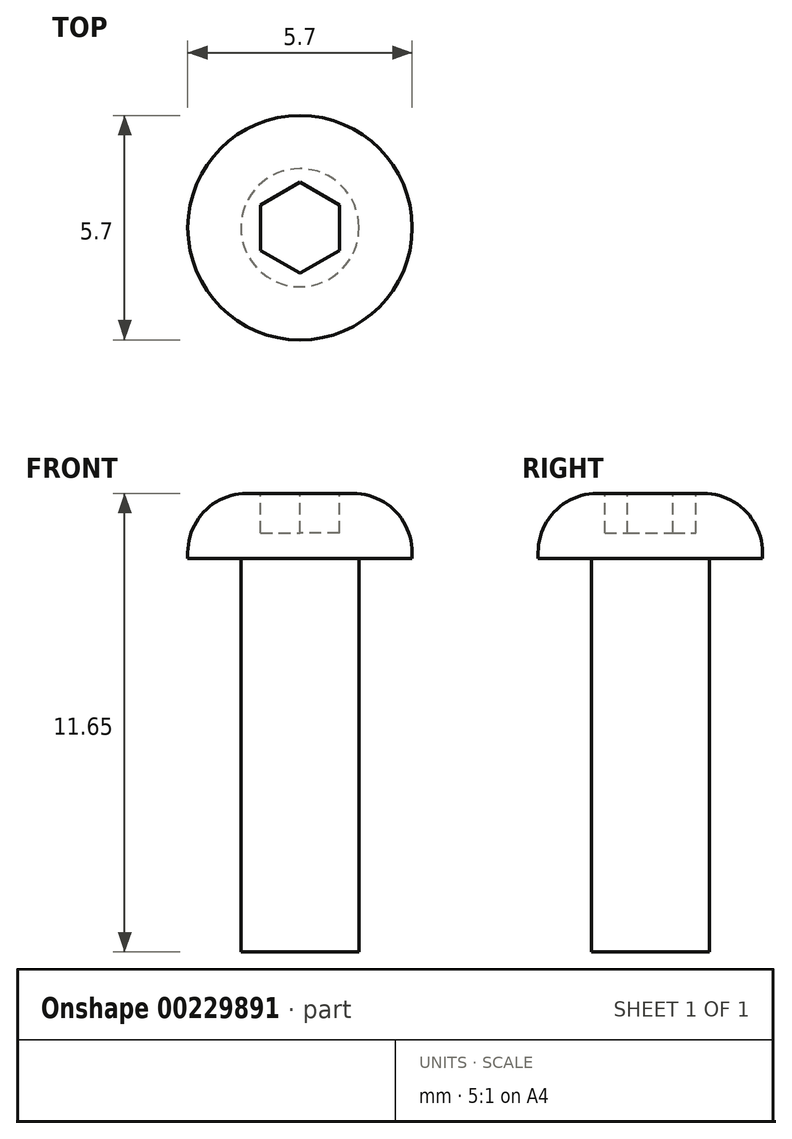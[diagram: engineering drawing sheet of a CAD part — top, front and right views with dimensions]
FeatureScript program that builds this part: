
annotation { "Feature Type Name" : "Feature", "Feature Type Description" : "" }
export const myFeature = defineFeature(function(context is Context, id is Id, definition is map)
    precondition{}
    {
        {
            var Q0;
            Q0=qCreatedBy(makeId("Top.planeOp"),FACE);
            var sketch = newSketch(context, id + "F0", { "sketchPlane" : qUnion([Q0])});
            skCircle(sketch, "E0", {"center": v(0, 0) * mm, "radius": 2.85 * mm});
            skCircle(sketch, "E1", {"center": v(0, 0) * mm, "radius": 1.5 * mm});
            skSolve(sketch);
        }
        {
            var Q0;
            Q0=makeQuery(id+"F0.imprint","IMPRINT",FACE,{"disambiguationData":[TD([[makeQuery(id+"F0.imprint","IMPRINT",EDGE,{"derivedFrom":sQuery(id+"F0.wireOp",EDGE,"E1")}),1.0]])]});
            extrude(context, id + "F1", {"entities" : qUnion([Q0]), "oppositeDirection" : true, "depth" : 10 * mm});
        }
        {
            var Q0;
            Q0 = qSketchRegion(id + "F0", true);
            var Q1;
            Q1=makeQuery(id+"F1.opExtrude","CAP_FACE",FACE,{"disambiguationData":[OSD([sQuery(id+"F0.wireOp",EDGE,"E1")])],"isStart":true});
            extrude(context, id + "F2", {"entities" : qUnion([Q0, Q1]), "operationType" : NewBodyOperationType.ADD, "depth" : 1.65 * mm});
        }
        {
            var Q0;
            {var subQ0=sQuery(id+"F0.wireOp",EDGE,"E1");Q0=makeQuery(id+"F2.boolean.opBoolean","MERGE",FACE,{"derivedFrom":[makeQuery(id+"F2.opExtrude","CAP_FACE",FACE,{"disambiguationData":[OSD([sQuery(id+"F0.wireOp",EDGE,"E0"),subQ0])],"isStart":false}),makeQuery(id+"F2.opExtrude","CAP_FACE",FACE,{"disambiguationData":[OSD([subQ0])],"isStart":false})]});}
            var sketch = newSketch(context, id + "F3", { "sketchPlane" : qUnion([Q0])});
            skCircle(sketch, "E2.cCircle", {"center": v(0, 0) * mm, "radius": 1 * mm, "construction": true});
            skLineSegment(sketch, "E2.0", {"start": v(-1, 0.58) * mm, "end": v(0, 1.15) * mm});
            skLineSegment(sketch, "E2.1", {"start": v(0, 1.15) * mm, "end": v(1, 0.58) * mm});
            skLineSegment(sketch, "E2.2", {"start": v(1, 0.58) * mm, "end": v(1, -0.58) * mm});
            skLineSegment(sketch, "E2.3", {"start": v(1, -0.58) * mm, "end": v(0, -1.15) * mm});
            skLineSegment(sketch, "E2.4", {"start": v(0, -1.15) * mm, "end": v(-1, -0.58) * mm});
            skLineSegment(sketch, "E2.5", {"start": v(-1, -0.58) * mm, "end": v(-1, 0.58) * mm});
            skPoint(sketch, "E2.0.midPoint", {"position": v(-0.5, 0.87) * mm});
            skSolve(sketch);
        }
        {
            var Q0;
            Q0 = qSketchRegion(id + "F3", true);
            extrude(context, id + "F4", {"entities" : qUnion([Q0]), "operationType" : NewBodyOperationType.REMOVE, "oppositeDirection" : true, "depth" : 1 * mm});
        }
        {
            var Q0;
            Q0=makeQuery(id+"F2.opExtrude","CAP_EDGE",EDGE,{"disambiguationData":[OSD([sQuery(id+"F0.wireOp",EDGE,"E0")])],"isStart":false});
            fillet(context, id + "F5", {"entities" : qUnion([Q0]), "radius" : 1.5 * mm, "tangentPropagation" : true, "allowEdgeOverflow" : false});
        }
    });
